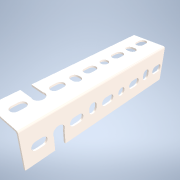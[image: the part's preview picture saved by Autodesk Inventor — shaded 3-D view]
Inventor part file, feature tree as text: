
AUTODESK INVENTOR PART (.ipt)
format: ipt  version: 2021 (Build 250183000, 183)  size: 216,064 bytes
history: mixed  units: in
note: dims shown in document units (in); Inventor stores cm internally (conversion verified against a paired STEP export)
features: extrude x2, sketch x2, other x1, imported_body x1
ambient origin geometry x8: Origin, YZ Plane, XZ Plane, XY Plane, X Axis, Y Axis, Z Axis, Center Point
bodies: Solid1 (imported_parasolid)
feature tree (6):
  other  "Other side cuts"
  extrude  "Extrusion1"  Depth=0.4331in
  extrude  "Extrusion2"  Depth=0.4331in
  sketch  "Sketch1"  dims[d0=0.4724in d1=0.4331in]
  sketch  "Sketch2"  dims[d2=0.0in d3=0.0in d4=0.4724in d5=0.4331in d6=0.0in d7=0.0in d8=0.0197in d9=0.0344in]
  imported_body  NMx_Import_Brep_tag  [imported B-rep: ~80 faces, bbox_mm=[40.1, 40.1, 177.8]]
